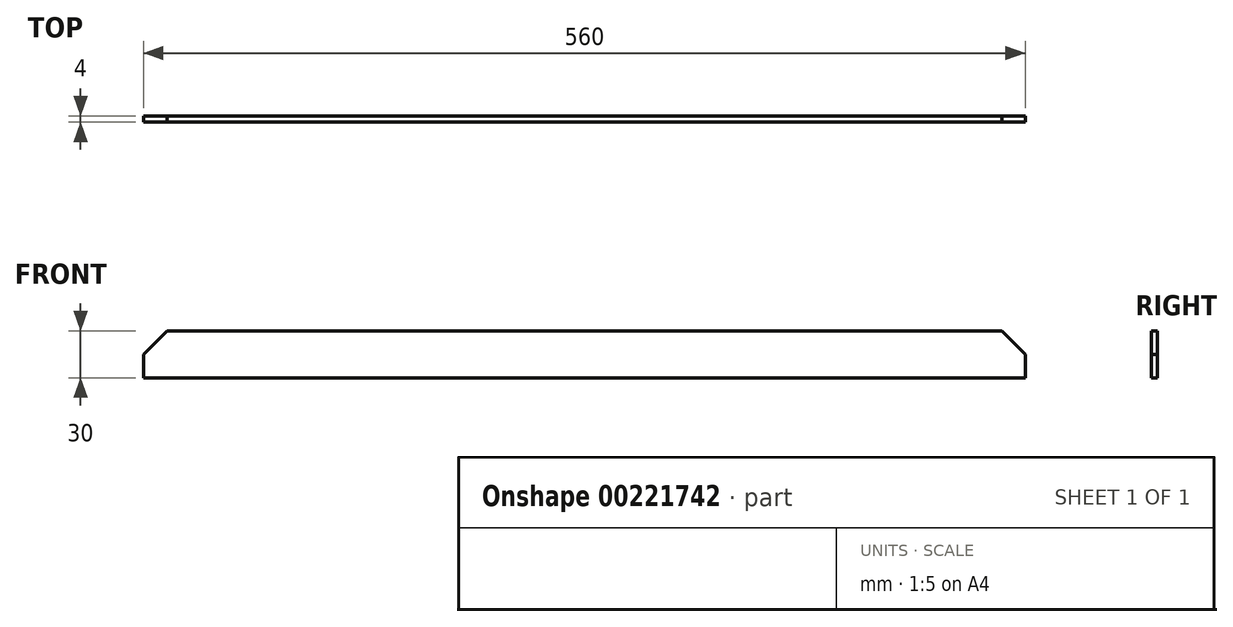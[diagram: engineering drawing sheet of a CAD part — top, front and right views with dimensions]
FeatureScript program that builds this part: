
annotation { "Feature Type Name" : "Feature", "Feature Type Description" : "" }
export const myFeature = defineFeature(function(context is Context, id is Id, definition is map)
    precondition{}
    {
        {
            var Q0;
            Q0=qCreatedBy(makeId("Front.planeOp"),FACE);
            var sketch = newSketch(context, id + "F0", { "sketchPlane" : qUnion([Q0])});
            skLineSegment(sketch, "E0.bottom", {"start": v(-280, -15) * mm, "end": v(280, -15) * mm});
            skLineSegment(sketch, "E0.top", {"start": v(-280, 15) * mm, "end": v(280, 15) * mm});
            skLineSegment(sketch, "E0.left", {"start": v(-280, -15) * mm, "end": v(-280, 15) * mm});
            skLineSegment(sketch, "E0.right", {"start": v(280, -15) * mm, "end": v(280, 15) * mm});
            skPoint(sketch, "E0.middle", {"position": v(0, 0) * mm});
            skSolve(sketch);
        }
        {
            var Q0;
            Q0 = qSketchRegion(id + "F0", true);
            extrude(context, id + "F1", {"entities" : qUnion([Q0]), "depth" : 4 * mm});
        }
        {
            var Q0;
            Q0=makeQuery(id+"F1.opExtrude","SWEPT_EDGE",EDGE,{"disambiguationData":[OSD([sQuery(id+"F0.wireOp",EDGE,"E0.top"),sQuery(id+"F0.wireOp",EDGE,"E0.left")])]});
            var Q1;
            Q1=makeQuery(id+"F1.opExtrude","SWEPT_EDGE",EDGE,{"disambiguationData":[OSD([sQuery(id+"F0.wireOp",EDGE,"E0.top"),sQuery(id+"F0.wireOp",EDGE,"E0.right")])]});
            chamfer(context, id + "F2", {"entities" : qUnion([Q0, Q1]), "width" : 15 * mm, "tangentPropagation" : true});
        }
    });
